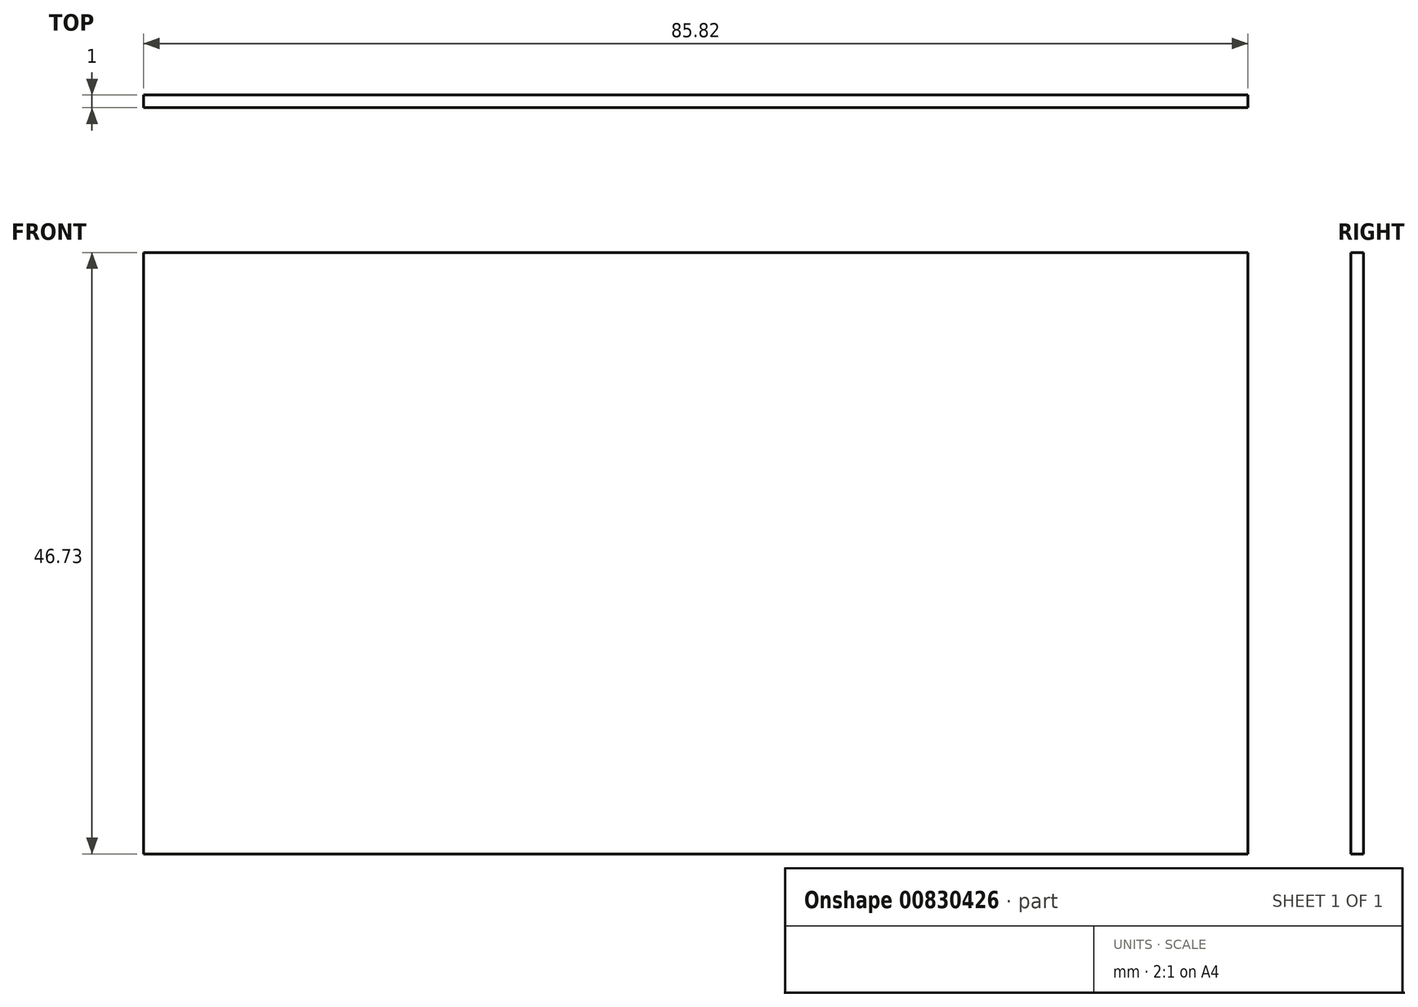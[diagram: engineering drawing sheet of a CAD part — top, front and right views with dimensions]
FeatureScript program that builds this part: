
annotation { "Feature Type Name" : "Feature", "Feature Type Description" : "" }
export const myFeature = defineFeature(function(context is Context, id is Id, definition is map)
    precondition{}
    {
        {
            var Q0;
            Q0=qCreatedBy(makeId("Front.planeOp"),FACE);
            var sketch = newSketch(context, id + "F0", { "sketchPlane" : qUnion([Q0])});
            skLineSegment(sketch, "E0.bottom", {"start": v(0, 0) * mm, "end": v(85.82, 0) * mm});
            skLineSegment(sketch, "E0.top", {"start": v(0, 46.73) * mm, "end": v(85.82, 46.73) * mm});
            skLineSegment(sketch, "E0.left", {"start": v(0, 0) * mm, "end": v(0, 46.73) * mm});
            skLineSegment(sketch, "E0.right", {"start": v(85.82, 0) * mm, "end": v(85.82, 46.73) * mm});
            skSolve(sketch);
        }
        {
            var Q0;
            Q0=makeQuery(id+"F0.imprint","IMPRINT",FACE,{"disambiguationData":[TD([[makeQuery(id+"F0.imprint","IMPRINT",EDGE,{"derivedFrom":sQuery(id+"F0.wireOp",EDGE,"E0.bottom")}),1.0]])]});
            extrude(context, id + "F1", {"entities" : qUnion([Q0]), "depth" : 1 * mm, "offsetDistance" : 25.4 * mm});
        }
    });
